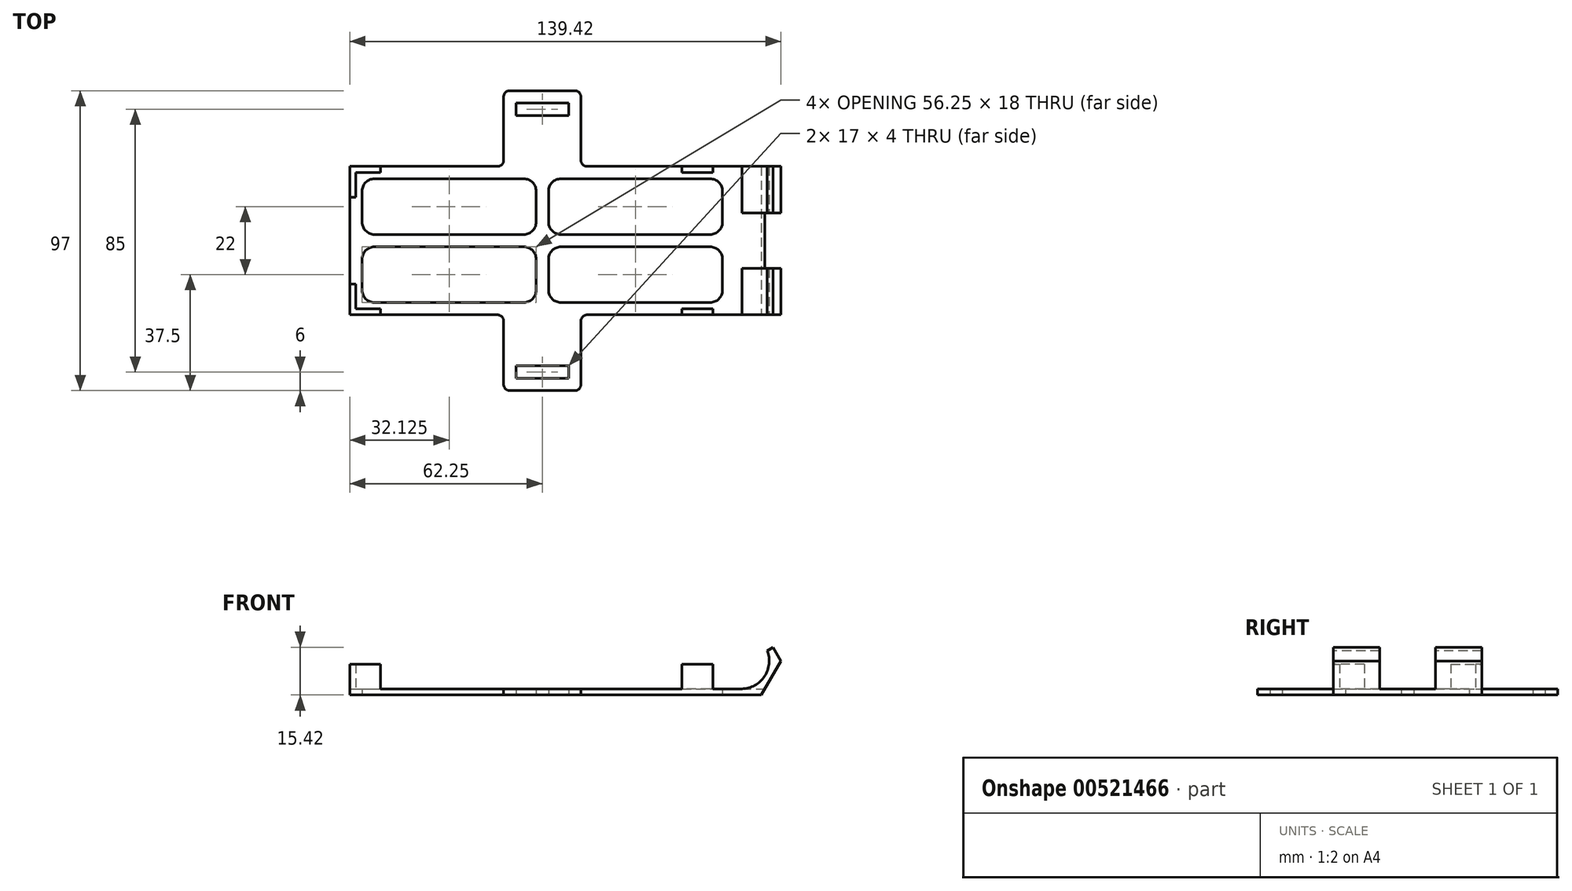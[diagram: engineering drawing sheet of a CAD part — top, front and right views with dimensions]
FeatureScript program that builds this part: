
annotation { "Feature Type Name" : "Feature", "Feature Type Description" : "" }
export const myFeature = defineFeature(function(context is Context, id is Id, definition is map)
    precondition{}
    {
        {
            assignVariable(context, id + "F0", {"name" : "batteryWidth", "anyValue" : 44});
        }
        {
            assignVariable(context, id + "F1", {"name" : "holderThickness", "anyValue" : 2});
        }
        {
            assignVariable(context, id + "F2", {"name" : "sideRise", "anyValue" : 8});
        }
        {
            var Q0;
            Q0=qCreatedBy(makeId("Top.planeOp"),FACE);
            var sketch = newSketch(context, id + "F3", { "sketchPlane" : qUnion([Q0])});
            skLineSegment(sketch, "E0.bottom", {"start": v(-66.5, 24) * mm, "end": v(-14.5, 24) * mm});
            skLineSegment(sketch, "E0.top", {"start": v(-66.5, -24) * mm, "end": v(-14.5, -24) * mm});
            skLineSegment(sketch, "E0.left", {"start": v(-66.5, 24) * mm, "end": v(-66.5, -24) * mm});
            skLineSegment(sketch, "E0.right", {"start": v(62.5, 24) * mm, "end": v(62.5, -24) * mm});
            skLineSegment(sketch, "E1.bottom", {"start": v(-14.75, 48.5) * mm, "end": v(6.25, 48.5) * mm});
            skLineSegment(sketch, "E1.left", {"start": v(-16.75, 46.5) * mm, "end": v(-16.75, 26) * mm});
            skLineSegment(sketch, "E1.right", {"start": v(8.25, 46.5) * mm, "end": v(8.25, 26) * mm});
            skLineSegment(sketch, "E2.bottom", {"start": v(-12.75, 44.5) * mm, "end": v(4.25, 44.5) * mm});
            skLineSegment(sketch, "E2.top", {"start": v(-12.75, 40.5) * mm, "end": v(4.25, 40.5) * mm});
            skLineSegment(sketch, "E2.left", {"start": v(-12.75, 44.5) * mm, "end": v(-12.75, 40.5) * mm});
            skLineSegment(sketch, "E2.right", {"start": v(4.25, 44.5) * mm, "end": v(4.25, 40.5) * mm});
            skLineSegment(sketch, "E3", {"start": v(-66.5, 0) * mm, "end": v(62.5, 0) * mm, "construction": true});
            skLineSegment(sketch, "E4.MirrorCS", {"start": v(-14.75, -48.5) * mm, "end": v(6.25, -48.5) * mm});
            skLineSegment(sketch, "E5.MirrorCS", {"start": v(4.25, -44.5) * mm, "end": v(4.25, -40.5) * mm});
            skLineSegment(sketch, "E6.MirrorCS", {"start": v(-12.75, -44.5) * mm, "end": v(-12.75, -40.5) * mm});
            skLineSegment(sketch, "E7.MirrorCS", {"start": v(-12.75, -40.5) * mm, "end": v(4.25, -40.5) * mm});
            skLineSegment(sketch, "E8.MirrorCS", {"start": v(-6.25, -24) * mm, "end": v(-2.25, -24) * mm});
            skLineSegment(sketch, "E9.MirrorCS", {"start": v(-12.75, -44.5) * mm, "end": v(4.25, -44.5) * mm});
            skLineSegment(sketch, "E10.MirrorCS", {"start": v(-16.75, -46.5) * mm, "end": v(-16.75, -26) * mm});
            skLineSegment(sketch, "E11.MirrorCS", {"start": v(8.25, -46.5) * mm, "end": v(8.25, -26) * mm});
            skLineSegment(sketch, "E12.0", {"start": v(-62.5, 20) * mm, "end": v(58.5, 20) * mm, "construction": true});
            skLineSegment(sketch, "E12.1", {"start": v(-62.5, 20) * mm, "end": v(-62.5, -20) * mm, "construction": true});
            skLineSegment(sketch, "E12.2", {"start": v(-62.5, -20) * mm, "end": v(58.5, -20) * mm, "construction": true});
            skLineSegment(sketch, "E12.3", {"start": v(58.5, 20) * mm, "end": v(58.5, -20) * mm, "construction": true});
            skLineSegment(sketch, "E13.bottom", {"start": v(-62.5, 2) * mm, "end": v(58.5, 2) * mm, "construction": true});
            skLineSegment(sketch, "E13.top", {"start": v(-62.5, -2) * mm, "end": v(58.5, -2) * mm, "construction": true});
            skLineSegment(sketch, "E13.left", {"start": v(-62.5, 2) * mm, "end": v(-62.5, -2) * mm, "construction": true});
            skLineSegment(sketch, "E13.right", {"start": v(58.5, 2) * mm, "end": v(58.5, -2) * mm, "construction": true});
            skLineSegment(sketch, "E14.left", {"start": v(-6.25, 24) * mm, "end": v(-6.25, -24) * mm, "construction": true});
            skLineSegment(sketch, "E14.right", {"start": v(-2.25, 24) * mm, "end": v(-2.25, -24) * mm, "construction": true});
            skLineSegment(sketch, "E15", {"start": v(-4.25, 24) * mm, "end": v(-4.25, -24) * mm, "construction": true});
            skLineSegment(sketch, "E16.bottom", {"start": v(-58.5, 20) * mm, "end": v(-10.25, 20) * mm});
            skLineSegment(sketch, "E16.top", {"start": v(-58.5, 2) * mm, "end": v(-10.25, 2) * mm});
            skLineSegment(sketch, "E16.left", {"start": v(-62.5, 16) * mm, "end": v(-62.5, 6) * mm});
            skLineSegment(sketch, "E16.right", {"start": v(-6.25, 16) * mm, "end": v(-6.25, 6) * mm});
            skPoint(sketch, "E17.visualSharp", {"position": v(-6.25, 2) * mm});
            skArc(sketch, "E17.filletArc", {"start": v(-10.25, 2) * mm, "mid": v(-7.42, 3.17) * mm, "end": v(-6.25, 6) * mm});
            skPoint(sketch, "E18.visualSharp", {"position": v(-62.5, 20) * mm});
            skArc(sketch, "E18.filletArc", {"start": v(-58.5, 20) * mm, "mid": v(-61.33, 18.83) * mm, "end": v(-62.5, 16) * mm});
            skPoint(sketch, "E19.visualSharp", {"position": v(-62.5, 2) * mm});
            skArc(sketch, "E19.filletArc", {"start": v(-62.5, 6) * mm, "mid": v(-61.33, 3.17) * mm, "end": v(-58.5, 2) * mm});
            skPoint(sketch, "E20.visualSharp", {"position": v(-6.25, 20) * mm});
            skArc(sketch, "E20.filletArc", {"start": v(-6.25, 16) * mm, "mid": v(-7.42, 18.83) * mm, "end": v(-10.25, 20) * mm});
            skLineSegment(sketch, "E21.MirrorCS", {"start": v(50, 2) * mm, "end": v(1.75, 2) * mm});
            skPoint(sketch, "E22.MirrorP", {"position": v(54, 2) * mm});
            skLineSegment(sketch, "E23.MirrorCS", {"start": v(50, 20) * mm, "end": v(1.75, 20) * mm});
            skPoint(sketch, "E24.MirrorP", {"position": v(-2.25, 20) * mm});
            skArc(sketch, "E25.MirrorCS", {"start": v(50, 20) * mm, "mid": v(52.83, 18.83) * mm, "end": v(54, 16) * mm});
            skLineSegment(sketch, "E26.MirrorCS", {"start": v(-2.25, 16) * mm, "end": v(-2.25, 6) * mm});
            skPoint(sketch, "E27.MirrorP", {"position": v(54, 20) * mm});
            skLineSegment(sketch, "E28.MirrorCS", {"start": v(54, 16) * mm, "end": v(54, 6) * mm});
            skArc(sketch, "E29.MirrorCS", {"start": v(54, 6) * mm, "mid": v(52.83, 3.17) * mm, "end": v(50, 2) * mm});
            skPoint(sketch, "E30.MirrorP", {"position": v(-2.25, 2) * mm});
            skArc(sketch, "E31.MirrorCS", {"start": v(-2.25, 16) * mm, "mid": v(-1.08, 18.83) * mm, "end": v(1.75, 20) * mm});
            skArc(sketch, "E32.MirrorCS", {"start": v(1.75, 2) * mm, "mid": v(-1.08, 3.17) * mm, "end": v(-2.25, 6) * mm});
            skArc(sketch, "E33.MirrorCS", {"start": v(50, -20) * mm, "mid": v(52.83, -18.83) * mm, "end": v(54, -16) * mm});
            skLineSegment(sketch, "E34.MirrorCS", {"start": v(-58.5, -2) * mm, "end": v(-10.25, -2) * mm});
            skLineSegment(sketch, "E35.MirrorCS", {"start": v(-58.5, -20) * mm, "end": v(-10.25, -20) * mm});
            skLineSegment(sketch, "E36.MirrorCS", {"start": v(50, -20) * mm, "end": v(1.75, -20) * mm});
            skLineSegment(sketch, "E37.MirrorCS", {"start": v(50, -2) * mm, "end": v(1.75, -2) * mm});
            skArc(sketch, "E38.MirrorCS", {"start": v(1.75, -2) * mm, "mid": v(-1.08, -3.17) * mm, "end": v(-2.25, -6) * mm});
            skPoint(sketch, "E39.MirrorP", {"position": v(-62.5, -2) * mm});
            skLineSegment(sketch, "E40.MirrorCS", {"start": v(54, -16) * mm, "end": v(54, -6) * mm});
            skArc(sketch, "E41.MirrorCS", {"start": v(-10.25, -2) * mm, "mid": v(-7.42, -3.17) * mm, "end": v(-6.25, -6) * mm});
            skLineSegment(sketch, "E42.MirrorCS", {"start": v(-6.25, -16) * mm, "end": v(-6.25, -6) * mm});
            skArc(sketch, "E43.MirrorCS", {"start": v(-58.5, -20) * mm, "mid": v(-61.33, -18.83) * mm, "end": v(-62.5, -16) * mm});
            skLineSegment(sketch, "E44.MirrorCS", {"start": v(-2.25, -16) * mm, "end": v(-2.25, -6) * mm});
            skLineSegment(sketch, "E45.MirrorCS", {"start": v(-62.5, -16) * mm, "end": v(-62.5, -6) * mm});
            skArc(sketch, "E46.MirrorCS", {"start": v(-2.25, -16) * mm, "mid": v(-1.08, -18.83) * mm, "end": v(1.75, -20) * mm});
            skArc(sketch, "E47.MirrorCS", {"start": v(54, -6) * mm, "mid": v(52.83, -3.17) * mm, "end": v(50, -2) * mm});
            skPoint(sketch, "E48.MirrorP", {"position": v(54, -2) * mm});
            skPoint(sketch, "E49.MirrorP", {"position": v(-62.5, -20) * mm});
            skPoint(sketch, "E50.MirrorP", {"position": v(-2.25, -20) * mm});
            skPoint(sketch, "E51.MirrorP", {"position": v(-2.25, -2) * mm});
            skPoint(sketch, "E52.MirrorP", {"position": v(-6.25, -20) * mm});
            skArc(sketch, "E53.MirrorCS", {"start": v(-6.25, -16) * mm, "mid": v(-7.42, -18.83) * mm, "end": v(-10.25, -20) * mm});
            skArc(sketch, "E54.MirrorCS", {"start": v(-62.5, -6) * mm, "mid": v(-61.33, -3.17) * mm, "end": v(-58.5, -2) * mm});
            skPoint(sketch, "E55.MirrorP", {"position": v(54, -20) * mm});
            skPoint(sketch, "E56.MirrorP", {"position": v(-6.25, -2) * mm});
            skPoint(sketch, "E57.visualSharp", {"position": v(-16.75, 48.5) * mm});
            skArc(sketch, "E57.filletArc", {"start": v(-14.75, 48.5) * mm, "mid": v(-16.16, 47.91) * mm, "end": v(-16.75, 46.5) * mm});
            skPoint(sketch, "E58.visualSharp", {"position": v(8.25, 48.5) * mm});
            skArc(sketch, "E58.filletArc", {"start": v(8.25, 46.5) * mm, "mid": v(7.66, 47.91) * mm, "end": v(6.25, 48.5) * mm});
            skLineSegment(sketch, "E59.trimOffspring", {"start": v(-6.25, 24) * mm, "end": v(-2.25, 24) * mm});
            skLineSegment(sketch, "E60.trimOffspring", {"start": v(14.5, 24) * mm, "end": v(62.5, 24) * mm});
            skPoint(sketch, "E61.visualSharp", {"position": v(-16.75, 24) * mm});
            skArc(sketch, "E61.filletArc", {"start": v(-18.75, 24) * mm, "mid": v(-17.34, 24.59) * mm, "end": v(-16.75, 26) * mm});
            skPoint(sketch, "E62.visualSharp", {"position": v(8.25, 24) * mm});
            skArc(sketch, "E62.filletArc", {"start": v(8.25, 26) * mm, "mid": v(8.84, 24.59) * mm, "end": v(10.25, 24) * mm});
            skLineSegment(sketch, "E63.trimOffspring", {"start": v(10.25, -24) * mm, "end": v(58.25, -24) * mm});
            skPoint(sketch, "E64.visualSharp", {"position": v(-16.75, -24) * mm});
            skArc(sketch, "E64.filletArc", {"start": v(-16.75, -26) * mm, "mid": v(-17.34, -24.59) * mm, "end": v(-18.75, -24) * mm});
            skPoint(sketch, "E65.visualSharp", {"position": v(8.25, -24) * mm});
            skArc(sketch, "E65.filletArc", {"start": v(10.25, -24) * mm, "mid": v(8.84, -24.59) * mm, "end": v(8.25, -26) * mm});
            skPoint(sketch, "E66.visualSharp", {"position": v(-16.75, -48.5) * mm});
            skArc(sketch, "E66.filletArc", {"start": v(-16.75, -46.5) * mm, "mid": v(-16.16, -47.91) * mm, "end": v(-14.75, -48.5) * mm});
            skPoint(sketch, "E67.visualSharp", {"position": v(8.25, -48.5) * mm});
            skArc(sketch, "E67.filletArc", {"start": v(6.25, -48.5) * mm, "mid": v(7.66, -47.91) * mm, "end": v(8.25, -46.5) * mm});
            skLineSegment(sketch, "E68", {"start": v(10.25, 24) * mm, "end": v(14.5, 24) * mm});
            skLineSegment(sketch, "E69", {"start": v(58.25, -24) * mm, "end": v(62.5, -24) * mm});
            skSolve(sketch);
        }
        {
            var Q0;
            Q0 = qSketchRegion(id + "F3", true);
            extrude(context, id + "F4", {"entities" : qUnion([Q0]), "depth" : (getVariable(context, 'holderThickness')) * mm, "offsetDistance" : 25 * mm});
        }
        {
            var Q0;
            Q0=qCreatedBy(makeId("Top.planeOp"),FACE);
            cPlane(context, id + "F5", {"entities" : qUnion([Q0]), "cplaneType" : CPlaneType.OFFSET, "offset" : (getVariable(context, 'holderThickness')) * mm, "width" : 150 * mm, "height" : 150 * mm});
        }
        {
            var Q0;
            Q0=qCreatedBy(id+"F5.planeOp",FACE);
            var sketch = newSketch(context, id + "F6", { "sketchPlane" : qUnion([Q0])});
            skLineSegment(sketch, "E70.bottom", {"start": v(-71, 24) * mm, "end": v(-14.5, 24) * mm, "construction": true});
            skLineSegment(sketch, "E70.top", {"start": v(-69, -24) * mm, "end": v(-14.5, -24) * mm, "construction": true});
            skLineSegment(sketch, "E70.left", {"start": v(-66.5, 24) * mm, "end": v(-66.5, -22) * mm, "construction": true});
            skLineSegment(sketch, "E70.right", {"start": v(50.85, 24) * mm, "end": v(50.85, 22) * mm, "construction": true});
            skLineSegment(sketch, "E71.bottom", {"start": v(-10.5, 48.5) * mm, "end": v(10.5, 48.5) * mm, "construction": true});
            skLineSegment(sketch, "E71.left", {"start": v(-12.5, 46.5) * mm, "end": v(-12.5, 26) * mm, "construction": true});
            skLineSegment(sketch, "E71.right", {"start": v(12.5, 46.5) * mm, "end": v(12.5, 26) * mm, "construction": true});
            skLineSegment(sketch, "E72.bottom", {"start": v(-8.5, 44.5) * mm, "end": v(8.5, 44.5) * mm, "construction": true});
            skLineSegment(sketch, "E72.top", {"start": v(-8.5, 40.5) * mm, "end": v(8.5, 40.5) * mm, "construction": true});
            skLineSegment(sketch, "E72.left", {"start": v(-8.5, 44.5) * mm, "end": v(-8.5, 40.5) * mm, "construction": true});
            skLineSegment(sketch, "E72.right", {"start": v(8.5, 44.5) * mm, "end": v(8.5, 40.5) * mm, "construction": true});
            skLineSegment(sketch, "E73", {"start": v(-71, 0) * mm, "end": v(71, 0) * mm, "construction": true});
            skLineSegment(sketch, "E74.MirrorCS", {"start": v(-10.5, -48.5) * mm, "end": v(10.5, -48.5) * mm, "construction": true});
            skLineSegment(sketch, "E75.MirrorCS", {"start": v(8.5, -44.5) * mm, "end": v(8.5, -40.5) * mm, "construction": true});
            skLineSegment(sketch, "E76.MirrorCS", {"start": v(-8.5, -44.5) * mm, "end": v(-8.5, -40.5) * mm, "construction": true});
            skLineSegment(sketch, "E77.MirrorCS", {"start": v(-8.5, -40.5) * mm, "end": v(8.5, -40.5) * mm, "construction": true});
            skLineSegment(sketch, "E78.MirrorCS", {"start": v(-2, -24) * mm, "end": v(2, -24) * mm, "construction": true});
            skLineSegment(sketch, "E79.MirrorCS", {"start": v(-8.5, -44.5) * mm, "end": v(8.5, -44.5) * mm, "construction": true});
            skLineSegment(sketch, "E80.MirrorCS", {"start": v(-12.5, -46.5) * mm, "end": v(-12.5, -26) * mm, "construction": true});
            skLineSegment(sketch, "E81.MirrorCS", {"start": v(12.5, -46.5) * mm, "end": v(12.5, -26) * mm, "construction": true});
            skLineSegment(sketch, "E82.0", {"start": v(-67, 20) * mm, "end": v(67, 20) * mm, "construction": true});
            skLineSegment(sketch, "E82.2", {"start": v(-62.75, -20) * mm, "end": v(71.25, -20) * mm, "construction": true});
            skLineSegment(sketch, "E83.bottom", {"start": v(-67, 2) * mm, "end": v(67, 2) * mm, "construction": true});
            skLineSegment(sketch, "E83.top", {"start": v(-67, -2) * mm, "end": v(67, -2) * mm, "construction": true});
            skLineSegment(sketch, "E84.left", {"start": v(-2, 24) * mm, "end": v(-2, -24) * mm, "construction": true});
            skLineSegment(sketch, "E84.right", {"start": v(2, 24) * mm, "end": v(2, -24) * mm, "construction": true});
            skLineSegment(sketch, "E85", {"start": v(0, 24) * mm, "end": v(0, -24) * mm, "construction": true});
            skPoint(sketch, "E86.visualSharp", {"position": v(-12.5, 48.5) * mm});
            skArc(sketch, "E86.filletArc", {"start": v(-10.5, 48.5) * mm, "mid": v(-11.91, 47.91) * mm, "end": v(-12.5, 46.5) * mm, "construction": true});
            skPoint(sketch, "E87.visualSharp", {"position": v(12.5, 48.5) * mm});
            skArc(sketch, "E87.filletArc", {"start": v(12.5, 46.5) * mm, "mid": v(11.91, 47.91) * mm, "end": v(10.5, 48.5) * mm, "construction": true});
            skLineSegment(sketch, "E88.trimOffspring", {"start": v(-2, 24) * mm, "end": v(2, 24) * mm, "construction": true});
            skLineSegment(sketch, "E89.trimOffspring", {"start": v(14.5, 24) * mm, "end": v(71, 24) * mm, "construction": true});
            skPoint(sketch, "E90.visualSharp", {"position": v(-12.5, 24) * mm});
            skArc(sketch, "E90.filletArc", {"start": v(-14.5, 24) * mm, "mid": v(-13.09, 24.59) * mm, "end": v(-12.5, 26) * mm, "construction": true});
            skPoint(sketch, "E91.visualSharp", {"position": v(12.5, 24) * mm});
            skArc(sketch, "E91.filletArc", {"start": v(12.5, 26) * mm, "mid": v(13.09, 24.59) * mm, "end": v(14.5, 24) * mm, "construction": true});
            skLineSegment(sketch, "E92.trimOffspring", {"start": v(14.5, -24) * mm, "end": v(71, -24) * mm, "construction": true});
            skPoint(sketch, "E93.visualSharp", {"position": v(-12.5, -24) * mm});
            skArc(sketch, "E93.filletArc", {"start": v(-12.5, -26) * mm, "mid": v(-13.09, -24.59) * mm, "end": v(-14.5, -24) * mm, "construction": true});
            skPoint(sketch, "E94.visualSharp", {"position": v(12.5, -24) * mm});
            skArc(sketch, "E94.filletArc", {"start": v(14.5, -24) * mm, "mid": v(13.09, -24.59) * mm, "end": v(12.5, -26) * mm, "construction": true});
            skPoint(sketch, "E95.visualSharp", {"position": v(-12.5, -48.5) * mm});
            skArc(sketch, "E95.filletArc", {"start": v(-12.5, -46.5) * mm, "mid": v(-11.91, -47.91) * mm, "end": v(-10.5, -48.5) * mm, "construction": true});
            skPoint(sketch, "E96.visualSharp", {"position": v(12.5, -48.5) * mm});
            skArc(sketch, "E96.filletArc", {"start": v(10.5, -48.5) * mm, "mid": v(11.91, -47.91) * mm, "end": v(12.5, -46.5) * mm, "construction": true});
            skLineSegment(sketch, "E97.bottom", {"start": v(-66.5, -14) * mm, "end": v(-64.5, -14) * mm});
            skLineSegment(sketch, "E97.top", {"start": v(-66.5, -24) * mm, "end": v(-64.5, -24) * mm});
            skLineSegment(sketch, "E97.left", {"start": v(-66.5, -14) * mm, "end": v(-66.5, -24) * mm});
            skLineSegment(sketch, "E97.right", {"start": v(-64.5, -14) * mm, "end": v(-64.5, -22) * mm});
            skLineSegment(sketch, "E98.bottom", {"start": v(-64.5, -24) * mm, "end": v(-56.5, -24) * mm});
            skLineSegment(sketch, "E98.top", {"start": v(-64.5, -22) * mm, "end": v(-56.5, -22) * mm});
            skLineSegment(sketch, "E98.right", {"start": v(-56.5, -24) * mm, "end": v(-56.5, -22) * mm});
            skPoint(sketch, "E99.orphan", {"position": v(-66.5, -24) * mm});
            skLineSegment(sketch, "E100.MirrorCS", {"start": v(-56.5, 24) * mm, "end": v(-56.5, 22) * mm});
            skLineSegment(sketch, "E101.MirrorCS", {"start": v(-64.5, 14) * mm, "end": v(-64.5, 22) * mm});
            skLineSegment(sketch, "E102.MirrorCS", {"start": v(-64.5, 22) * mm, "end": v(-56.5, 22) * mm});
            skLineSegment(sketch, "E103.MirrorCS", {"start": v(-64.5, 24) * mm, "end": v(-56.5, 24) * mm});
            skPoint(sketch, "E104.MirrorP", {"position": v(-66.5, 24) * mm});
            skLineSegment(sketch, "E105.MirrorCS", {"start": v(-66.5, 24) * mm, "end": v(-64.5, 24) * mm});
            skLineSegment(sketch, "E106.MirrorCS", {"start": v(-66.5, 14) * mm, "end": v(-64.5, 14) * mm});
            skLineSegment(sketch, "E107.MirrorCS", {"start": v(-66.5, 14) * mm, "end": v(-66.5, 24) * mm});
            skLineSegment(sketch, "E108.MirrorCS", {"start": v(50.85, 24) * mm, "end": v(48.85, 24) * mm});
            skLineSegment(sketch, "E109.MirrorCS", {"start": v(40.85, 24) * mm, "end": v(40.85, 22) * mm});
            skLineSegment(sketch, "E110.MirrorCS", {"start": v(50.85, -24) * mm, "end": v(48.85, -24) * mm});
            skLineSegment(sketch, "E111.MirrorCS", {"start": v(50.85, 22) * mm, "end": v(50.85, 24) * mm});
            skPoint(sketch, "E112.MirrorP", {"position": v(50.85, 24) * mm});
            skLineSegment(sketch, "E113.MirrorCS", {"start": v(40.85, -24) * mm, "end": v(40.85, -22) * mm});
            skLineSegment(sketch, "E114.MirrorCS", {"start": v(50.85, -22) * mm, "end": v(50.85, -24) * mm});
            skLineSegment(sketch, "E115.MirrorCS", {"start": v(48.85, 24) * mm, "end": v(40.85, 24) * mm});
            skPoint(sketch, "E116.MirrorP", {"position": v(50.85, -24) * mm});
            skLineSegment(sketch, "E117.MirrorCS", {"start": v(48.85, -24) * mm, "end": v(40.85, -24) * mm});
            skLineSegment(sketch, "E118", {"start": v(40.85, 22) * mm, "end": v(50.85, 22) * mm});
            skLineSegment(sketch, "E119.trimOffspring", {"start": v(50.85, 14) * mm, "end": v(50.85, -14) * mm, "construction": true});
            skLineSegment(sketch, "E120", {"start": v(40.85, -22) * mm, "end": v(50.85, -22) * mm});
            skLineSegment(sketch, "E121.trimOffspring", {"start": v(50.85, -22) * mm, "end": v(50.85, -24) * mm, "construction": true});
            skSolve(sketch);
        }
        {
            var Q0;
            Q0 = qSketchRegion(id + "F6", true);
            extrude(context, id + "F7", {"entities" : qUnion([Q0]), "operationType" : NewBodyOperationType.ADD, "depth" : (getVariable(context, 'sideRise')) * mm, "offsetDistance" : 25 * mm});
        }
        {
            var Q0;
            Q0=makeQuery(id+"F7.boolean.opBoolean","MERGE",FACE,{"derivedFrom":[makeQuery(id+"F4.opExtrude","SWEPT_FACE",FACE,{"disambiguationData":[OSD([sQuery(id+"F3.wireOp",EDGE,"E63.trimOffspring")])]}),makeQuery(id+"F7.opExtrude","SWEPT_FACE",FACE,{"disambiguationData":[OSD([sQuery(id+"F6.wireOp",EDGE,"E110.MirrorCS"),sQuery(id+"F6.wireOp",EDGE,"E117.MirrorCS")])]})]});
            cPlane(context, id + "F8", {"entities" : qUnion([Q0]), "cplaneType" : CPlaneType.OFFSET, "offset" : 0 * mm, "width" : 150 * mm, "height" : 150 * mm});
        }
        {
            var Q0;
            Q0=qCreatedBy(id+"F8.planeOp",FACE);
            var sketch = newSketch(context, id + "F9", { "sketchPlane" : qUnion([Q0])});
            skArc(sketch, "E122", {"start": v(60.25, 2) * mm, "mid": v(67.58, 6) * mm, "end": v(68.46, 14.32) * mm});
            skLineSegment(sketch, "E123.0", {"start": v(72.92, 10.99) * mm, "end": v(66.57, 0) * mm});
            skLineSegment(sketch, "E123.1", {"start": v(66.57, 0) * mm, "end": v(60.25, 0) * mm});
            skLineSegment(sketch, "E123.5", {"start": v(70.37, 15.42) * mm, "end": v(72.92, 10.99) * mm});
            skPoint(sketch, "E123.0.midPoint", {"position": v(69.75, 5.5) * mm});
            skLineSegment(sketch, "E124", {"start": v(60.25, 2) * mm, "end": v(60.25, 0) * mm});
            skLineSegment(sketch, "E125", {"start": v(68.46, 14.32) * mm, "end": v(70.37, 15.42) * mm});
            skLineSegment(sketch, "E126", {"start": v(69.1, 11) * mm, "end": v(68.74, 0) * mm, "construction": true});
            skSolve(sketch);
        }
        {
            var Q0;
            Q0 = qSketchRegion(id + "F9", true);
            extrude(context, id + "F10", {"entities" : qUnion([Q0]), "operationType" : NewBodyOperationType.ADD, "oppositeDirection" : true, "depth" : (getVariable(context, 'batteryWidth') + (2 * getVariable(context, 'holderThickness'))) * mm, "offsetDistance" : 25 * mm});
        }
        {
            var Q0;
            Q0=qCreatedBy(id+"F5.planeOp",FACE);
            var sketch = newSketch(context, id + "F11", { "sketchPlane" : qUnion([Q0])});
            skLineSegment(sketch, "E127.bottom", {"start": v(59.35, 9) * mm, "end": v(74.35, 9) * mm});
            skLineSegment(sketch, "E127.top", {"start": v(59.35, -9) * mm, "end": v(74.35, -9) * mm});
            skLineSegment(sketch, "E127.left", {"start": v(59.35, 9) * mm, "end": v(59.35, -9) * mm});
            skLineSegment(sketch, "E127.right", {"start": v(74.35, 9) * mm, "end": v(74.35, -9) * mm});
            skSolve(sketch);
        }
        {
            var Q0;
            Q0 = qSketchRegion(id + "F11", true);
            extrude(context, id + "F12", {"entities" : qUnion([Q0]), "operationType" : NewBodyOperationType.REMOVE, "depth" : 25 * mm, "offsetDistance" : 25 * mm});
        }
    });
